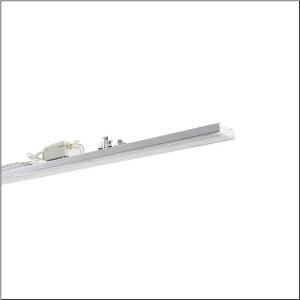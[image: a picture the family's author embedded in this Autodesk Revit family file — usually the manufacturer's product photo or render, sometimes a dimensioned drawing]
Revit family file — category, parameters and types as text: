
# Revit family: licross_r__21_recessed_ho_52tl12cn495m_a1ad
name_source: partatom
category: Lighting Fixtures
units: mm (PartAtom-declared; Revit-internal decimal feet)

## family parameters
Cut with Voids When Loaded = No
Host = Face
Light Source = No
Part Type = Normal
Room Calculation Point = No
Round Connector Dimension = Use Diameter
Shared = No

## types (1)
- --- (1 x LED, 10000 lm, 53 W, 4000K)
    Apparent Load = 53 VA
    CIE Flux Codes = 69 91 98 100 100
    Color Rendering = 80
    Color Temperature = 4000K
    Default Elevation = 1800 mm
    Description = Licross® 21 Recessed HO, luminaire insert, of sheet steel, galvanised, coil coated, white, length: 1.500mm, width: 66mm, height: 67mm, LED rated luminous flux: 9.990lm, light colour: 840, control gear: ON/OFF Multilumen, CLOi, control gear: ECG Multilumen, with plug, 3-pole, with phase selection, mains connection: 220..240V, AC, 50/60Hz, halogen-free wiring, primary optical cover: cover, of PMMA, light emission: direct distribution, primary light characteristic: symmetric, protection rating (complete): IP40, insulation class (complete): insulation class I (protective earthing), certification: CE, ENEC, VDE, UKCA, protection symbol: D if used in an environment without relevant dust loads with corresponding accessories, impact resistance: IK06, permissible ambient temperature for indoor applications: -35..+35°C, corresponds to IFS (International Featured Standards) requirements for safety and quality in the food industry, reducing of maximum allowable ambient temperature of 5°C with ceiling mounting, LABS conformity tested according to VDMA 24364:2018-05, packaging unit: 1 piece
    Height = 58 mm
    Lamp = 1 x LED
    Lamp Light Flux = 10000 lm
    Lamp Power = 53 W
    Lamp count = 1
    Length = 1500 mm
    Luminous efficacy = 189 lm/W
    Manufacturer = Siteco
    ModVariant = No
    Model = 52TL12CN495M
    Mounting Place = Ceiling
    Mounting Type = Pendant
    Number of Poles = 1
    OnlyDefault = Yes
    Power Factor = 1
    Product Name = Licross® 21 Recessed HO
    Product group = luminaire insert
    ProductGroupID = 901
    Protection Class = Protection class I
    Protection Degree = IP 40
    RLX_Detail_Level = 1
    RLX_Emergency_Light_Flux = 0 lm
    RLX_Emergency_Type = 0
    RLX_Emergency_Type_DB = No
    RlxData = <blob elided: 22345 chars, md5=5e480a0c>
    Socket = socket
    Standby Power = 0 W
    System Light Flux = 10000 lm
    System Power = 53 W
    Type Comments = factory setting: luminous flux: 100 % | (A | C | E) | 125 mA
    Type Image = l_1296930.jpg
    URL = http://relux.com
    VarID = @adj_039985
    Voltage = 0 V
    Weight = 0.00 kg
    Width = 66 mm

## geometry (parser evidence)
native form markers: Blend x4, Sweep x10
no freeform markers — native parametric forms only
